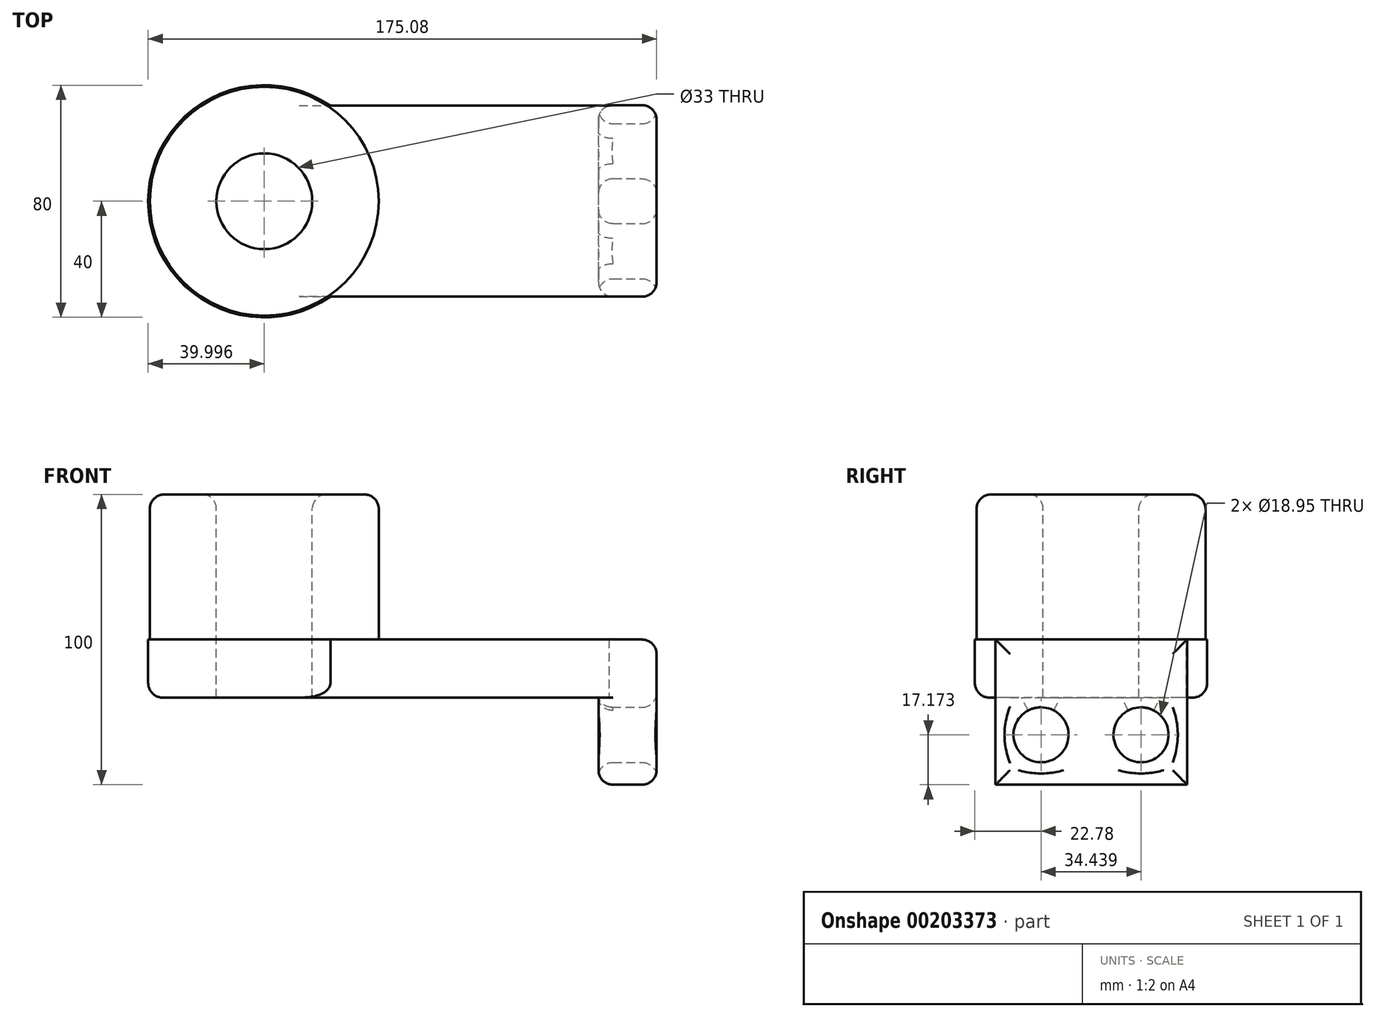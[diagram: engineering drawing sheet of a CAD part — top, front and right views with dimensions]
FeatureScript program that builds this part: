
annotation { "Feature Type Name" : "Feature", "Feature Type Description" : "" }
export const myFeature = defineFeature(function(context is Context, id is Id, definition is map)
    precondition{}
    {
        {
            var Q0;
            Q0=qCreatedBy(makeId("Top.planeOp"),FACE);
            var sketch = newSketch(context, id + "F0", { "sketchPlane" : qUnion([Q0])});
            skLineSegment(sketch, "E0.bottom", {"start": v(-59.79, 32.9) * mm, "end": v(52.54, 32.9) * mm});
            skLineSegment(sketch, "E0.top", {"start": v(-59.79, -32.9) * mm, "end": v(52.54, -32.9) * mm});
            skLineSegment(sketch, "E0.left", {"start": v(-59.79, 32.9) * mm, "end": v(-59.79, -32.9) * mm});
            skLineSegment(sketch, "E0.right", {"start": v(52.54, 32.9) * mm, "end": v(52.54, -32.9) * mm});
            skArc(sketch, "E1", {"start": v(-59.79, 32.9) * mm, "mid": v(-122.54, 0) * mm, "end": v(-59.79, -32.9) * mm});
            skCircle(sketch, "E2", {"center": v(-82.54, 0) * mm, "radius": 16.5 * mm});
            skSolve(sketch);
        }
        {
            var Q0;
            Q0 = qSketchRegion(id + "F0", true);
            extrude(context, id + "F1", {"entities" : qUnion([Q0]), "oppositeDirection" : true, "depth" : 20 * mm});
        }
        {
            var Q0;
            Q0=makeQuery(id+"F1.opExtrude","CAP_FACE",FACE,{"disambiguationData":[OSD([sQuery(id+"F0.wireOp",EDGE,"E0.bottom"),sQuery(id+"F0.wireOp",EDGE,"E0.top"),sQuery(id+"F0.wireOp",EDGE,"E0.right"),sQuery(id+"F0.wireOp",EDGE,"E1"),sQuery(id+"F0.wireOp",EDGE,"E2")])],"isStart":true});
            var sketch = newSketch(context, id + "F2", { "sketchPlane" : qUnion([Q0])});
            skCircle(sketch, "E3", {"center": v(-82.54, 0) * mm, "radius": 39.42 * mm});
            skCircle(sketch, "E4", {"center": v(-82.54, 0) * mm, "radius": 16.5 * mm});
            skSolve(sketch);
        }
        {
            var Q0;
            Q0 = qSketchRegion(id + "F2", true);
            extrude(context, id + "F3", {"entities" : qUnion([Q0]), "operationType" : NewBodyOperationType.ADD, "depth" : 50 * mm});
        }
        {
            var Q0;
            Q0=makeQuery(id+"F1.opExtrude","SWEPT_FACE",FACE,{"disambiguationData":[OSD([sQuery(id+"F0.wireOp",EDGE,"E0.right")])]});
            var sketch = newSketch(context, id + "F4", { "sketchPlane" : qUnion([Q0])});
            skLineSegment(sketch, "E5.bottom", {"start": v(-32.9, 0) * mm, "end": v(33.1, 0) * mm});
            skLineSegment(sketch, "E5.top", {"start": v(-32.9, -50) * mm, "end": v(33.1, -50) * mm});
            skLineSegment(sketch, "E5.left", {"start": v(-32.9, 0) * mm, "end": v(-32.9, -50) * mm});
            skLineSegment(sketch, "E5.right", {"start": v(33.1, 0) * mm, "end": v(33.1, -50) * mm});
            skLineSegment(sketch, "E6", {"start": v(0, 0) * mm, "end": v(0, -50) * mm});
            skCircle(sketch, "E7", {"center": v(-17.22, -32.83) * mm, "radius": 9.47 * mm});
            skCircle(sketch, "E8.MirrorC", {"center": v(17.22, -32.83) * mm, "radius": 9.47 * mm});
            skSolve(sketch);
        }
        {
            var Q0;
            Q0 = qSketchRegion(id + "F4", true);
            extrude(context, id + "F5", {"entities" : qUnion([Q0]), "operationType" : NewBodyOperationType.ADD, "oppositeDirection" : true, "depth" : 15 * mm});
        }
        {
            var Q0;
            Q0 = qSketchRegion(id + "F4", true);
            extrude(context, id + "F6", {"entities" : qUnion([Q0]), "operationType" : NewBodyOperationType.ADD, "oppositeDirection" : true, "depth" : 20 * mm});
        }
        {
            var Q0;
            Q0=makeQuery(id+"F5.boolean.opBoolean","MERGE",EDGE,{"derivedFrom":[makeQuery(id+"F1.opExtrude","CAP_EDGE",EDGE,{"disambiguationData":[OSD([sQuery(id+"F0.wireOp",EDGE,"E0.right")])],"isStart":true}),makeQuery(id+"F5.opExtrude","CAP_EDGE",EDGE,{"disambiguationData":[OSD([sQuery(id+"F4.wireOp",EDGE,"E5.bottom")])],"isStart":true})]});
            var Q1;
            Q1=makeQuery(id+"F5.opExtrude","CAP_EDGE",EDGE,{"disambiguationData":[OSD([sQuery(id+"F4.wireOp",EDGE,"E7")])],"isStart":true});
            var Q2;
            Q2=makeQuery(id+"F5.opExtrude","CAP_EDGE",EDGE,{"disambiguationData":[OSD([sQuery(id+"F4.wireOp",EDGE,"E5.top")])],"isStart":true});
            var Q3;
            Q3=makeQuery(id+"F5.opExtrude","CAP_EDGE",EDGE,{"disambiguationData":[OSD([sQuery(id+"F4.wireOp",EDGE,"E5.right")])],"isStart":true});
            var Q4;
            Q4=makeQuery(id+"F5.boolean.opBoolean","MERGE",EDGE,{"derivedFrom":[makeQuery(id+"F1.opExtrude","SWEPT_EDGE",EDGE,{"disambiguationData":[OSD([sQuery(id+"F0.wireOp",EDGE,"E0.top"),sQuery(id+"F0.wireOp",EDGE,"E0.right")])]}),makeQuery(id+"F5.opExtrude","CAP_EDGE",EDGE,{"disambiguationData":[OSD([sQuery(id+"F4.wireOp",EDGE,"E5.left")])],"isStart":true})]});
            var Q5;
            Q5=makeQuery(id+"F6.opExtrude","CAP_EDGE",EDGE,{"disambiguationData":[OSD([sQuery(id+"F4.wireOp",EDGE,"E7")])],"isStart":false});
            var Q6;
            {var subQ0=sQuery(id+"F4.wireOp",EDGE,"E8.MirrorC");Q6=makeQuery(id+"F6.boolean.opBoolean","MERGE",FACE,{"derivedFrom":[makeQuery(id+"F5.opExtrude","SWEPT_FACE",FACE,{"disambiguationData":[OSD([subQ0])]}),makeQuery(id+"F6.opExtrude","SWEPT_FACE",FACE,{"disambiguationData":[OSD([subQ0])]})]});}
            var Q7;
            Q7=makeQuery(id+"F6.opExtrude","CAP_EDGE",EDGE,{"disambiguationData":[OSD([sQuery(id+"F4.wireOp",EDGE,"E5.top")])],"isStart":false});
            var Q8;
            Q8=makeQuery(id+"F6.opExtrude","CAP_EDGE",EDGE,{"disambiguationData":[OSD([sQuery(id+"F4.wireOp",EDGE,"E5.left")])],"isStart":false});
            var Q9;
            Q9=makeQuery(id+"F6.opExtrude","CAP_EDGE",EDGE,{"disambiguationData":[OSD([sQuery(id+"F4.wireOp",EDGE,"E5.right")])],"isStart":false});
            var Q10;
            Q10=makeQuery(id+"F3.opExtrude","CAP_EDGE",EDGE,{"disambiguationData":[OSD([sQuery(id+"F2.wireOp",EDGE,"E4")])],"isStart":false});
            var Q11;
            Q11=makeQuery(id+"F3.opExtrude","CAP_EDGE",EDGE,{"disambiguationData":[OSD([sQuery(id+"F2.wireOp",EDGE,"E3")])],"isStart":false});
            var Q12;
            Q12=makeQuery(id+"F3.boolean.opBoolean","SPLIT",EDGE,{"disambiguationData":[OD(1.0)],"derivedFrom":makeQuery(id+"F3.opExtrude","CAP_EDGE",EDGE,{"disambiguationData":[OSD([sQuery(id+"F2.wireOp",EDGE,"E3")])],"isStart":true})});
            var Q13;
            Q13=makeQuery(id+"F1.opExtrude","CAP_EDGE",EDGE,{"disambiguationData":[OSD([sQuery(id+"F0.wireOp",EDGE,"E1")])],"isStart":false});
            fillet(context, id + "F7", {"entities" : qUnion([Q0, Q1, Q2, Q3, Q4, Q5, Q6, Q7, Q8, Q9, Q10, Q11, Q12, Q13]), "radius" : 5 * mm, "tangentPropagation" : true, "allowEdgeOverflow" : false});
        }
    });
